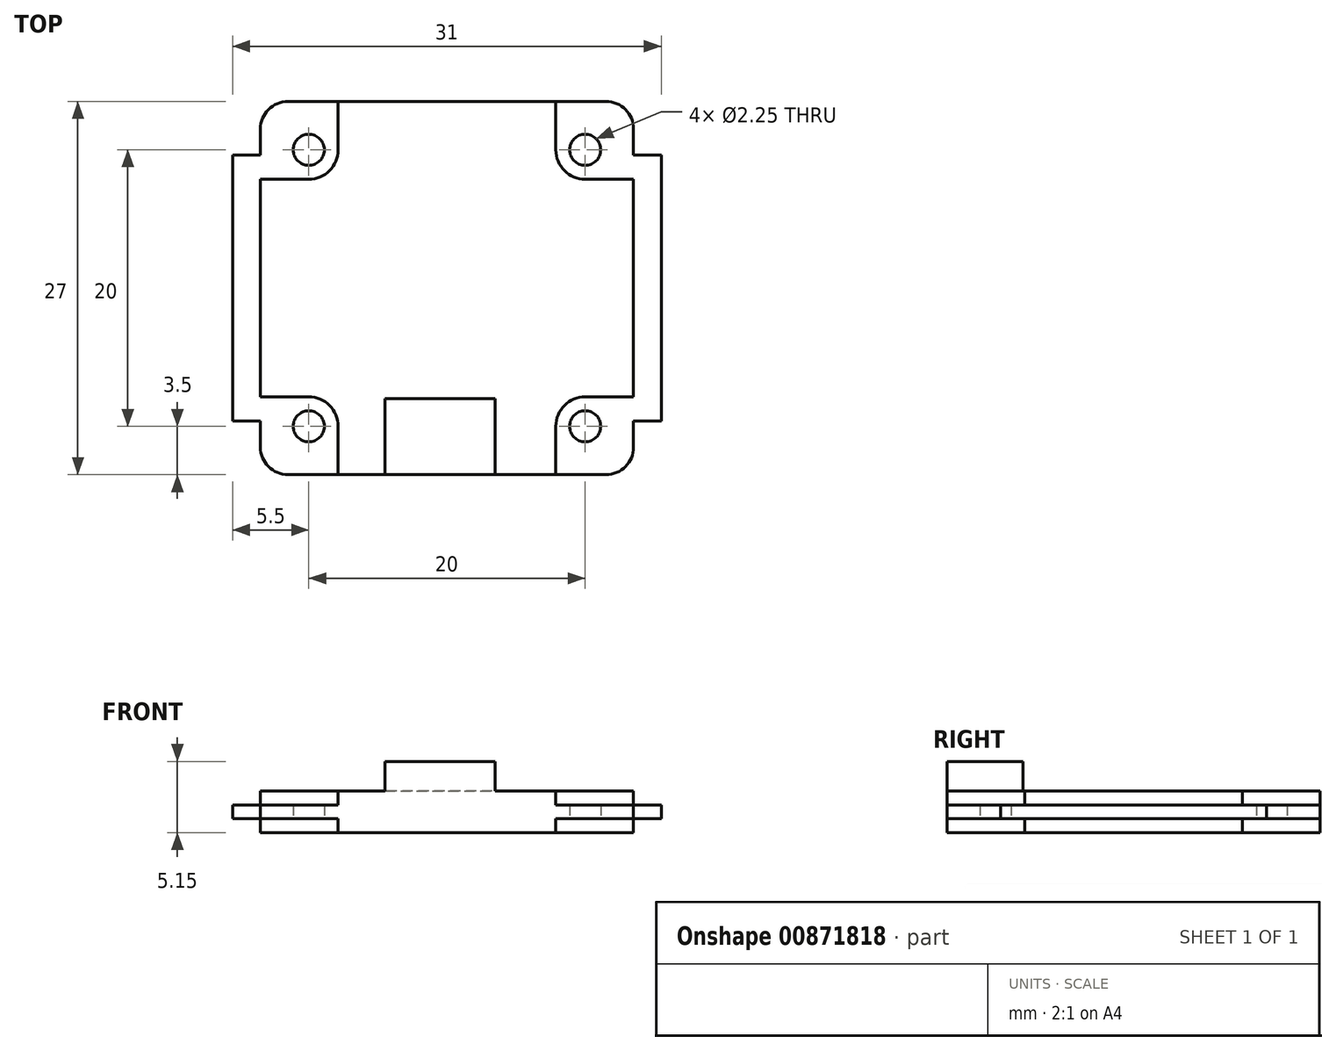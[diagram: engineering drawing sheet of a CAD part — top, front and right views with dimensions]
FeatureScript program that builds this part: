
annotation { "Feature Type Name" : "Feature", "Feature Type Description" : "" }
export const myFeature = defineFeature(function(context is Context, id is Id, definition is map)
    precondition{}
    {
        {
            var Q0;
            Q0=qCreatedBy(makeId("Top.planeOp"),FACE);
            var sketch = newSketch(context, id + "F0", { "sketchPlane" : qUnion([Q0])});
            skLineSegment(sketch, "E0.bottom", {"start": v(13.5, 13.5) * mm, "end": v(-13.5, 13.5) * mm});
            skLineSegment(sketch, "E0.top", {"start": v(13.5, -13.5) * mm, "end": v(-13.5, -13.5) * mm});
            skLineSegment(sketch, "E0.left", {"start": v(13.5, 13.5) * mm, "end": v(13.5, -13.5) * mm});
            skLineSegment(sketch, "E0.right", {"start": v(-13.5, 13.5) * mm, "end": v(-13.5, -13.5) * mm});
            skPoint(sketch, "E0.middle", {"position": v(0, 0) * mm});
            skLineSegment(sketch, "E1.bottom", {"start": v(10, 10) * mm, "end": v(-10, 10) * mm, "construction": true});
            skLineSegment(sketch, "E1.top", {"start": v(10, -10) * mm, "end": v(-10, -10) * mm, "construction": true});
            skLineSegment(sketch, "E1.left", {"start": v(10, 10) * mm, "end": v(10, -10) * mm, "construction": true});
            skLineSegment(sketch, "E1.right", {"start": v(-10, 10) * mm, "end": v(-10, -10) * mm, "construction": true});
            skLineSegment(sketch, "E2.bottom", {"start": v(-13.5, 9.63) * mm, "end": v(-15.5, 9.63) * mm});
            skLineSegment(sketch, "E2.top", {"start": v(-13.5, -9.62) * mm, "end": v(-15.5, -9.62) * mm});
            skLineSegment(sketch, "E2.left", {"start": v(-13.5, 9.63) * mm, "end": v(-13.5, -9.63) * mm});
            skLineSegment(sketch, "E2.right", {"start": v(-15.5, 9.63) * mm, "end": v(-15.5, -9.63) * mm});
            skPoint(sketch, "E3", {"position": v(-15.5, 0) * mm});
            skLineSegment(sketch, "E4.MirrorCS", {"start": v(13.5, 9.63) * mm, "end": v(15.5, 9.63) * mm});
            skLineSegment(sketch, "E5.MirrorCS", {"start": v(15.5, 9.63) * mm, "end": v(15.5, -9.63) * mm});
            skLineSegment(sketch, "E6.MirrorCS", {"start": v(13.5, -9.62) * mm, "end": v(15.5, -9.62) * mm});
            skSolve(sketch);
        }
        {
            var Q0;
            Q0 = qSketchRegion(id + "F0", true);
            extrude(context, id + "F1", {"entities" : qUnion([Q0]), "depth" : 1 * mm, "offsetDistance" : 25 * mm});
        }
        {
            var Q0;
            Q0=makeQuery(id+"F1.opExtrude","SWEPT_EDGE",EDGE,{"disambiguationData":[OSD([sQuery(id+"F0.wireOp",EDGE,"E0.top"),sQuery(id+"F0.wireOp",EDGE,"E0.right")])]});
            var Q1;
            Q1=makeQuery(id+"F1.opExtrude","SWEPT_EDGE",EDGE,{"disambiguationData":[OSD([sQuery(id+"F0.wireOp",EDGE,"E0.top"),sQuery(id+"F0.wireOp",EDGE,"E0.left")])]});
            var Q2;
            Q2=makeQuery(id+"F1.opExtrude","SWEPT_EDGE",EDGE,{"disambiguationData":[OSD([sQuery(id+"F0.wireOp",EDGE,"E0.bottom"),sQuery(id+"F0.wireOp",EDGE,"E0.left")])]});
            var Q3;
            Q3=makeQuery(id+"F1.opExtrude","SWEPT_EDGE",EDGE,{"disambiguationData":[OSD([sQuery(id+"F0.wireOp",EDGE,"E0.bottom"),sQuery(id+"F0.wireOp",EDGE,"E0.right")])]});
            fillet(context, id + "F2", {"entities" : qUnion([Q0, Q1, Q2, Q3]), "radius" : 2 * mm, "tangentPropagation" : true, "allowEdgeOverflow" : false});
        }
        {
            var Q0;
            Q0=sQuery(id+"F0.wireOp",VERTEX,"E1.bottom.end");
            var Q1;
            Q1=sQuery(id+"F0.wireOp",VERTEX,"E1.bottom.start");
            var Q2;
            Q2=sQuery(id+"F0.wireOp",VERTEX,"E1.top.start");
            var Q3;
            Q3=sQuery(id+"F0.wireOp",VERTEX,"E1.top.end");
            var Q4;
            Q4=makeQuery(id+"F1.opExtrude","SWEPT_BODY",BODY,{"disambiguationData":[OSD([sQuery(id+"F0.wireOp",EDGE,"E0.bottom"),sQuery(id+"F0.wireOp",EDGE,"E0.top"),sQuery(id+"F0.wireOp",EDGE,"E0.left"),sQuery(id+"F0.wireOp",EDGE,"E0.right")])]});
            hole(context, id + "F3", {"style" : HoleStyle.SIMPLE, "endStyle" : HoleEndStyle.THROUGH, "oppositeDirection" : true, "holeDiameter" : 2.25 * mm, "majorDiameter" : 5 * mm, "isTappedThrough" : true, "tappedDepth" : 12 * mm, "tapClearance" : 3, "locations" : qUnion([Q0, Q1, Q2, Q3]), "scope" : qUnion([Q4])});
        }
        {
            var Q0;
            Q0=makeQuery(id+"F1.opExtrude","CAP_FACE",FACE,{"disambiguationData":[OSD([sQuery(id+"F0.wireOp",EDGE,"E0.bottom"),sQuery(id+"F0.wireOp",EDGE,"E0.top"),sQuery(id+"F0.wireOp",EDGE,"E0.left"),sQuery(id+"F0.wireOp",EDGE,"E0.right"),sQuery(id+"F0.wireOp",EDGE,"E2.bottom"),sQuery(id+"F0.wireOp",EDGE,"E2.top"),sQuery(id+"F0.wireOp",EDGE,"E2.right"),sQuery(id+"F0.wireOp",EDGE,"E4.MirrorCS"),sQuery(id+"F0.wireOp",EDGE,"E5.MirrorCS"),sQuery(id+"F0.wireOp",EDGE,"E6.MirrorCS")])],"isStart":false});
            var sketch = newSketch(context, id + "F4", { "sketchPlane" : qUnion([Q0])});
            skLineSegment(sketch, "E7.bottom", {"start": v(-4.5, -13.5) * mm, "end": v(3.5, -13.5) * mm});
            skLineSegment(sketch, "E7.top", {"start": v(-4.5, -8) * mm, "end": v(3.5, -8) * mm});
            skLineSegment(sketch, "E7.left", {"start": v(-4.5, -13.5) * mm, "end": v(-4.5, -8) * mm});
            skLineSegment(sketch, "E7.right", {"start": v(3.5, -13.5) * mm, "end": v(3.5, -8) * mm});
            skSolve(sketch);
        }
        {
            var Q0;
            Q0 = qSketchRegion(id + "F4", true);
            extrude(context, id + "F5", {"entities" : qUnion([Q0]), "operationType" : NewBodyOperationType.ADD, "depth" : 3.15 * mm, "offsetDistance" : 25 * mm});
        }
        {
            var Q0;
            Q0=qCreatedBy(makeId("Top.planeOp"),FACE);
            var sketch = newSketch(context, id + "F6", { "sketchPlane" : qUnion([Q0])});
            skLineSegment(sketch, "E8.0", {"start": v(7.88, -13.5) * mm, "end": v(-7.88, -13.5) * mm});
            skLineSegment(sketch, "E9.0", {"start": v(-13.5, 7.88) * mm, "end": v(-13.5, -7.88) * mm});
            skLineSegment(sketch, "E10", {"start": v(-7.88, -13.5) * mm, "end": v(-7.88, -10) * mm});
            skCircle(sketch, "E11.0", {"center": v(-10, -10) * mm, "radius": 1.13 * mm, "construction": true});
            skArc(sketch, "E12", {"start": v(-7.88, -10) * mm, "mid": v(-8.5, -8.5) * mm, "end": v(-10, -7.88) * mm});
            skLineSegment(sketch, "E13", {"start": v(-10, -7.88) * mm, "end": v(-13.5, -7.88) * mm});
            skLineSegment(sketch, "E14.MirrorCS", {"start": v(10, -7.88) * mm, "end": v(13.5, -7.88) * mm});
            skArc(sketch, "E15.MirrorCS", {"start": v(7.88, -10) * mm, "mid": v(8.5, -8.5) * mm, "end": v(10, -7.88) * mm});
            skLineSegment(sketch, "E16.MirrorCS", {"start": v(7.88, -13.5) * mm, "end": v(7.88, -10) * mm});
            skLineSegment(sketch, "E17.MirrorCS", {"start": v(-10, 7.88) * mm, "end": v(-13.5, 7.88) * mm});
            skArc(sketch, "E18.MirrorCS", {"start": v(-7.88, 10) * mm, "mid": v(-8.5, 8.5) * mm, "end": v(-10, 7.88) * mm});
            skLineSegment(sketch, "E19.MirrorCS", {"start": v(-7.88, 13.5) * mm, "end": v(-7.88, 10) * mm});
            skLineSegment(sketch, "E20.MirrorCS", {"start": v(7.88, 13.5) * mm, "end": v(7.88, 10) * mm});
            skArc(sketch, "E21.MirrorCS", {"start": v(7.88, 10) * mm, "mid": v(8.5, 8.5) * mm, "end": v(10, 7.88) * mm});
            skLineSegment(sketch, "E22.MirrorCS", {"start": v(10, 7.88) * mm, "end": v(13.5, 7.88) * mm});
            skLineSegment(sketch, "E23.0", {"start": v(13.5, 7.88) * mm, "end": v(13.5, -7.88) * mm});
            skLineSegment(sketch, "E24.MirrorCS", {"start": v(7.88, 13.5) * mm, "end": v(-7.88, 13.5) * mm});
            skSolve(sketch);
        }
        {
            var Q0;
            Q0 = qSketchRegion(id + "F6", true);
            extrude(context, id + "F7", {"entities" : qUnion([Q0]), "operationType" : NewBodyOperationType.ADD, "depth" : 2 * mm, "offsetDistance" : 25 * mm, "hasSecondDirection" : true, "secondDirectionOppositeDirection" : true, "secondDirectionDepth" : 1 * mm});
        }
    });
